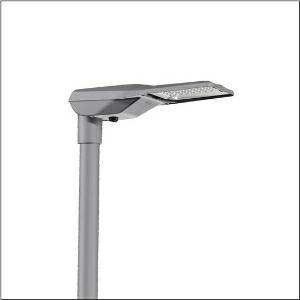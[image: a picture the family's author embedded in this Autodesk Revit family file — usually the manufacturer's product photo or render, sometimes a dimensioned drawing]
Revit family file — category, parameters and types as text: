
# Revit family: streetlight_sl_21_iq_mini___p0_5a_5xe2v31u08jb_c08b
name_source: partatom
category: Lighting Fixtures
units: mm (PartAtom-declared; Revit-internal decimal feet)

## family parameters
Cut with Voids When Loaded = No
Host = Face
Light Source = No
Part Type = Normal
Room Calculation Point = No
Round Connector Dimension = Use Diameter
Shared = No

## types (1)
- --- (1 x LED, 11020 lm, 72.5 W, 3000K)
    Apparent Load = 73 VA
    CIE Flux Codes = 37 73 96 100 100
    Color Rendering = 70
    Color Temperature = 3000K
    Default Elevation = 1800 mm
    Description = Streetlight SL 21 iQ mini, mast luminaire, primary light control with lens, of PMMA, primary optical cover: cover, of toughened safety glass, transparent, light distribution: P0.5a, light emission: direct distribution, primary light characteristic: asymmetric, installation type: post-top, side-entry, LED, High Power LED, rated luminous flux: 11.020lm, luminous efficacy: 152lm/W, light colour: 730, colour temperature: 3000K, control gear: iQ-Street Remote, D4i with power reduction, control: pre-setting: logarithmic dimming characteristic, Street-Remote, Auto-Match, Temp-Guard, Lumen-Switch, Night-Set, Smart-Wire, Light-Fading, Desk-Remote (wireless, voltage-free reading and setting of iQ features in the workshop via application-optimized NFC function/RFID function), optimised constant luminous flux control (CLO 2.0), mains connection: 220..240V, AC, 50/60Hz, start of lifetime: 73W, end of service life: 76W, reduction: 33W, luminaire housing, of diecast aluminium, powder-coated, Siteco® metallic grey (DB 702S), corrosivity category C5 mid according to DIN EN ISO 12944, please order mast flange separately, inclination adjustable: 0°, 5°, 10°, 15°, sealing non-destructively replaceable, multi-level sealing system, length: 628mm, width: 235mm, height: 110mm, mast flange for spigot size: 42mm (side-entry): 5XC10008XM4, 60/48mm (side-entry/post-top): 5XC10108XM2, 76/60mm (side-entry/post-top): 5XC10108XM1, mounting height: 4..8m, Smart Interface below, protection rating (complete): IP66, insulation class (complete): insulation class II (safety insulation), certification: CE, ENEC, ENEC+, VDE, impact resistance: IK10, permissible operating ambient temperature for outdoor applications: -40..+50°C, standard-compliant lighting for roads and squares, packaging unit: 1 piece

Light Distribution: P0.5a
    Height = 110 mm
    Lamp = 1 x LED
    Lamp Light Flux = 11020 lm
    Lamp Power = 72.5 W
    Lamp count = 1
    Length = 625 mm
    Luminous efficacy = 152 lm/W
    Manufacturer = Siteco
    ModVariant = No
    Model = 5XE2V31U08JB
    Number of Poles = 1
    OnlyDefault = Yes
    Power Factor = 1
    Product Name = Streetlight SL 21 iQ mini | P0.5a
    Product group = mast luminaire | pylon top
    ProductGroupID = 6100
    Protection Class = Protection class II
    Protection Degree = IP 66
    RLX_Detail_Level = 1
    RLX_Emergency_Light_Flux = 0 lm
    RLX_Emergency_Type = 0
    RLX_Emergency_Type_DB = No
    RlxData = <blob elided: 26269 chars, md5=5911511a>
    Socket = socket
    Standby Power = 0 W
    System Light Flux = 11020 lm
    System Power = 73 W
    Type Comments = factory setting: luminous flux: 100 % | dim-lin: 254 | 755 mA
    Type Image = l_1003516.jpg
    URL = http://relux.com
    VarID = @adj_069464
    Voltage = 0 V
    Weight = 0.00 kg
    Width = 234 mm

## geometry (parser evidence)
native form markers: Blend x4, Sweep x10
no freeform markers — native parametric forms only
